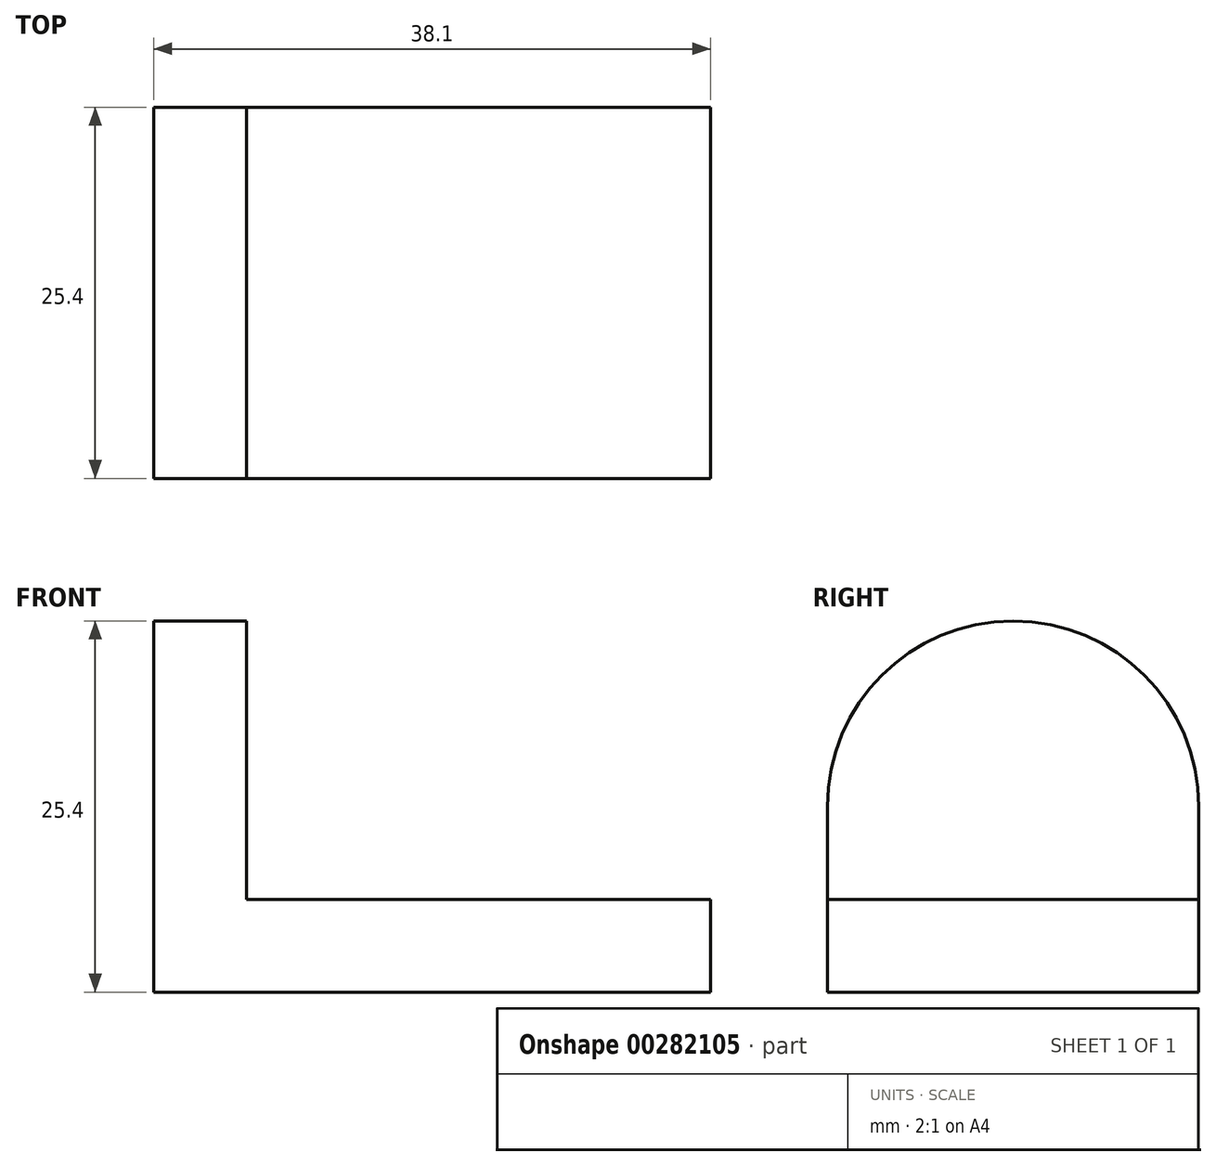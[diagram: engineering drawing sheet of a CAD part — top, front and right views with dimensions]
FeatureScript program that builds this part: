
annotation { "Feature Type Name" : "Feature", "Feature Type Description" : "" }
export const myFeature = defineFeature(function(context is Context, id is Id, definition is map)
    precondition{}
    {
        {
            var Q0;
            Q0=qCreatedBy(makeId("Top.planeOp"),FACE);
            var sketch = newSketch(context, id + "F0", { "sketchPlane" : qUnion([Q0])});
            skLineSegment(sketch, "E0", {"start": v(0, 0) * mm, "end": v(38.1, 0) * mm});
            skLineSegment(sketch, "E1", {"start": v(38.1, 0) * mm, "end": v(38.1, 25.4) * mm});
            skLineSegment(sketch, "E2", {"start": v(38.1, 25.4) * mm, "end": v(0, 25.4) * mm});
            skLineSegment(sketch, "E3", {"start": v(0, 25.4) * mm, "end": v(0, 0) * mm});
            skSolve(sketch);
        }
        {
            var Q0;
            Q0 = qSketchRegion(id + "F0", true);
            extrude(context, id + "F1", {"entities" : qUnion([Q0]), "depth" : 6.35 * mm});
        }
        {
            var Q0;
            Q0=qCreatedBy(makeId("Right.planeOp"),FACE);
            var sketch = newSketch(context, id + "F2", { "sketchPlane" : qUnion([Q0])});
            skLineSegment(sketch, "E4", {"start": v(0, 6.35) * mm, "end": v(0, 12.7) * mm});
            skLineSegment(sketch, "E5", {"start": v(25.4, 6.35) * mm, "end": v(25.4, 12.7) * mm});
            skArc(sketch, "E6", {"start": v(25.4, 12.7) * mm, "mid": v(12.7, 25.4) * mm, "end": v(0, 12.7) * mm});
            skLineSegment(sketch, "E7", {"start": v(0, 6.35) * mm, "end": v(25.4, 6.35) * mm});
            skSolve(sketch);
        }
        {
            var Q0;
            Q0 = qSketchRegion(id + "F2", true);
            extrude(context, id + "F3", {"entities" : qUnion([Q0]), "operationType" : NewBodyOperationType.ADD, "depth" : 6.35 * mm});
        }
    });
